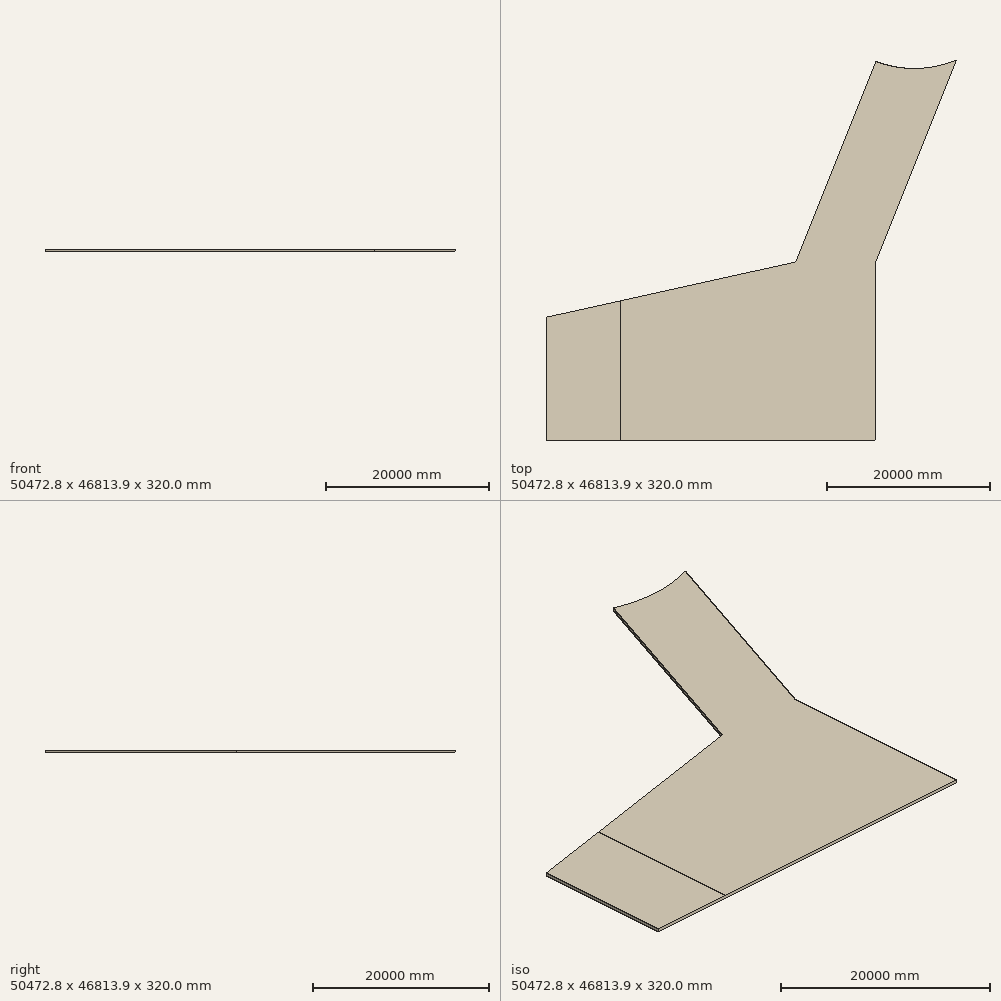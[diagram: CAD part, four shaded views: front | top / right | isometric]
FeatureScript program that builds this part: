
annotation { "Feature Type Name" : "Feature", "Feature Type Description" : "" }
export const myFeature = defineFeature(function(context is Context, id is Id, definition is map)
    precondition{}
    {
        {
            var Q0;
            Q0=qCreatedBy(makeId("Top.planeOp"),FACE);
            var sketch = newSketch(context, id + "F0", { "sketchPlane" : qUnion([Q0])});
            skLineSegment(sketch, "E0", {"start": v(0, 0) * mm, "end": v(-40483.54, 0) * mm});
            skLineSegment(sketch, "E1", {"start": v(-40483.54, 0) * mm, "end": v(-40483.54, 15179.04) * mm});
            skLineSegment(sketch, "E2", {"start": v(-40483.54, 15179.04) * mm, "end": v(-9791.26, 21981.51) * mm});
            skLineSegment(sketch, "E3", {"start": v(0, 0) * mm, "end": v(0, 21838.92) * mm});
            skLineSegment(sketch, "E4", {"start": v(0, 21838.92) * mm, "end": v(9989.27, 46813.89) * mm});
            skLineSegment(sketch, "E5", {"start": v(-9791.26, 21981.51) * mm, "end": v(81.43, 46664.99) * mm});
            skLineSegment(sketch, "E6", {"start": v(0, 21838.92) * mm, "end": v(0, 35478.5) * mm, "construction": true});
            skLineSegment(sketch, "E7", {"start": v(-9791.26, 21981.51) * mm, "end": v(-37025.38, 21981.51) * mm, "construction": true});
            skArc(sketch, "E8", {"start": v(81.43, 46664.99) * mm, "mid": v(5049.27, 45813.45) * mm, "end": v(9989.27, 46813.89) * mm});
            skSolve(sketch);
        }
        {
            var Q0;
            Q0=makeQuery(id+"F0.imprint","IMPRINT",FACE,{"disambiguationData":[TD([[makeQuery(id+"F0.imprint","IMPRINT",EDGE,{"derivedFrom":sQuery(id+"F0.wireOp",EDGE,"E0")}),-1.0]])]});
            var Q1;
            Q1=sQuery(id+"F0.wireOp",EDGE,"E5");
            var Q2;
            Q2=sQuery(id+"F0.wireOp",EDGE,"E8");
            var Q3;
            Q3=sQuery(id+"F0.wireOp",EDGE,"E4");
            var Q4;
            Q4=sQuery(id+"F0.wireOp",EDGE,"E3");
            var Q5;
            Q5=sQuery(id+"F0.wireOp",EDGE,"E0");
            var Q6;
            Q6=sQuery(id+"F0.wireOp",EDGE,"E1");
            var Q7;
            Q7=sQuery(id+"F0.wireOp",EDGE,"E2");
            extrude(context, id + "F1", {"entities" : qUnion([Q0]), "surfaceEntities" : qUnion([Q1, Q2, Q3, Q4, Q5, Q6, Q7]), "depth" : -304.8 * mm});
        }
        {
            var Q0;
            Q0=makeQuery(id+"F1.opExtrude","CAP_FACE",FACE,{"disambiguationData":[OSD([sQuery(id+"F0.wireOp",EDGE,"E0"),sQuery(id+"F0.wireOp",EDGE,"E1"),sQuery(id+"F0.wireOp",EDGE,"E2"),sQuery(id+"F0.wireOp",EDGE,"E3"),sQuery(id+"F0.wireOp",EDGE,"E4"),sQuery(id+"F0.wireOp",EDGE,"E5"),sQuery(id+"F0.wireOp",EDGE,"E8")])],"isStart":false});
            var sketch = newSketch(context, id + "F2", { "sketchPlane" : qUnion([Q0])});
            skLineSegment(sketch, "E9", {"start": v(-31339.54, 0) * mm, "end": v(-31339.54, -17205.67) * mm});
            skSolve(sketch);
        }
        {
            var Q0;
            {var subQ0=sQuery(id+"F2.wireOp",EDGE,"E9");Q0=makeQuery(id+"F2.imprint","IMPRINT",FACE,{"disambiguationData":[TD([[makeQuery(id+"F2.imprint","IMPRINT",EDGE,{"derivedFrom":subQ0}),-1.0]])]});}
            extrude(context, id + "F3", {"entities" : qUnion([Q0]), "operationType" : NewBodyOperationType.ADD, "oppositeDirection" : true, "depth" : 320.04 * mm});
        }
    });
